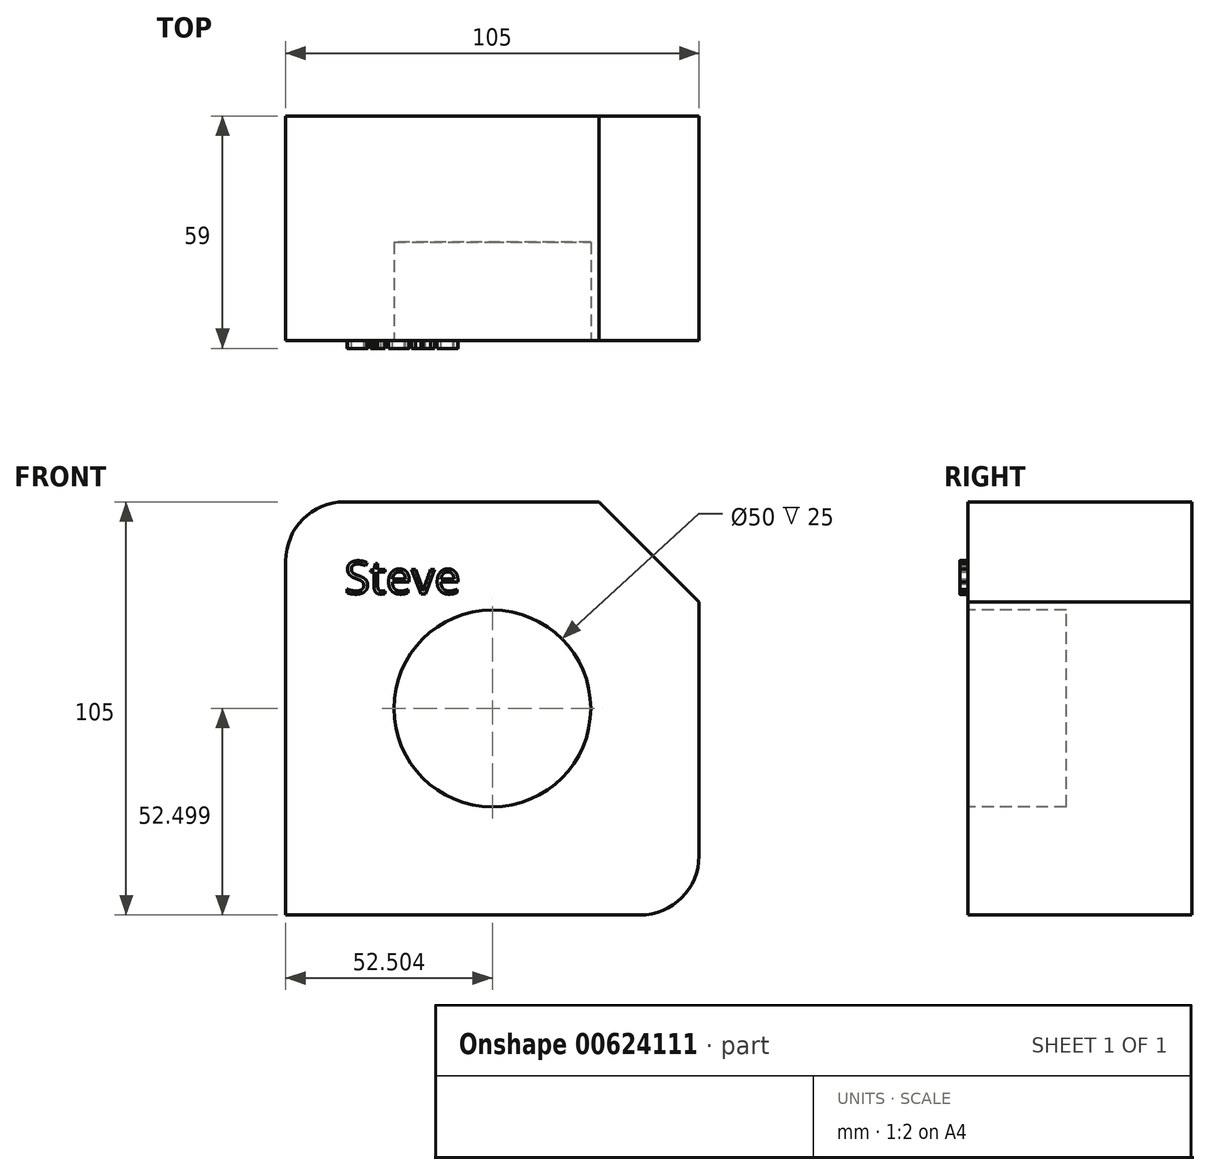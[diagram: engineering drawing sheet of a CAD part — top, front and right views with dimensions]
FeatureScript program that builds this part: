
annotation { "Feature Type Name" : "Feature", "Feature Type Description" : "" }
export const myFeature = defineFeature(function(context is Context, id is Id, definition is map)
    precondition{}
    {
        {
            var Q0;
            Q0=qCreatedBy(makeId("Front.planeOp"),FACE);
            var sketch = newSketch(context, id + "F0", { "sketchPlane" : qUnion([Q0])});
            skLineSegment(sketch, "E0.bottom", {"start": v(-33.87, 50.29) * mm, "end": v(30.73, 50.29) * mm});
            skLineSegment(sketch, "E0.top", {"start": v(-48.87, -54.71) * mm, "end": v(41.13, -54.71) * mm});
            skLineSegment(sketch, "E0.left", {"start": v(-48.87, 35.29) * mm, "end": v(-48.87, -54.71) * mm});
            skLineSegment(sketch, "E0.right", {"start": v(56.13, 24.88) * mm, "end": v(56.13, -39.71) * mm});
            skPoint(sketch, "E1.visualSharp", {"position": v(-48.87, 50.29) * mm});
            skArc(sketch, "E1.filletArc", {"start": v(-33.87, 50.29) * mm, "mid": v(-44.47, 45.9) * mm, "end": v(-48.87, 35.29) * mm});
            skPoint(sketch, "E2.visualSharp", {"position": v(56.13, -54.71) * mm});
            skArc(sketch, "E2.filletArc", {"start": v(41.13, -54.71) * mm, "mid": v(51.74, -50.32) * mm, "end": v(56.13, -39.71) * mm});
            skLineSegment(sketch, "E3", {"start": v(30.73, 50.29) * mm, "end": v(56.13, 24.88) * mm});
            skPoint(sketch, "E4.orphan", {"position": v(56.13, 50.29) * mm});
            skSolve(sketch);
        }
        {
            var Q0;
            Q0 = qSketchRegion(id + "F0", true);
            extrude(context, id + "F1", {"entities" : qUnion([Q0]), "depth" : 57 * mm, "offsetDistance" : 25 * mm});
        }
        {
            var Q0;
            Q0=makeQuery(id+"F1.opExtrude","CAP_FACE",FACE,{"disambiguationData":[OSD([sQuery(id+"F0.wireOp",EDGE,"E0.bottom"),sQuery(id+"F0.wireOp",EDGE,"E0.top"),sQuery(id+"F0.wireOp",EDGE,"E0.left"),sQuery(id+"F0.wireOp",EDGE,"E0.right"),sQuery(id+"F0.wireOp",EDGE,"E1.filletArc"),sQuery(id+"F0.wireOp",EDGE,"E2.filletArc"),sQuery(id+"F0.wireOp",EDGE,"E3")])],"isStart":false});
            var sketch = newSketch(context, id + "F2", { "sketchPlane" : qUnion([Q0])});
            skCircle(sketch, "E5", {"center": v(3.63, -2.21) * mm, "radius": 25 * mm});
            skSolve(sketch);
        }
        {
            var Q0;
            Q0 = qSketchRegion(id + "F2", true);
            extrude(context, id + "F3", {"entities" : qUnion([Q0]), "operationType" : NewBodyOperationType.REMOVE, "oppositeDirection" : true, "depth" : 25 * mm, "offsetDistance" : 25 * mm});
        }
        {
            var Q0;
            Q0=makeQuery(id+"F1.opExtrude","CAP_FACE",FACE,{"disambiguationData":[OSD([sQuery(id+"F0.wireOp",EDGE,"E0.bottom"),sQuery(id+"F0.wireOp",EDGE,"E0.top"),sQuery(id+"F0.wireOp",EDGE,"E0.left"),sQuery(id+"F0.wireOp",EDGE,"E0.right"),sQuery(id+"F0.wireOp",EDGE,"E1.filletArc"),sQuery(id+"F0.wireOp",EDGE,"E2.filletArc"),sQuery(id+"F0.wireOp",EDGE,"E3")])],"isStart":false});
            var sketch = newSketch(context, id + "F4", { "sketchPlane" : qUnion([Q0])});
            skText(sketch, "E6", { "text": "Steve", "fontName": "OpenSans-Regular.ttf"});
            const initialGuessF4  = {"E6": [-0.03387, 0.02692, 1, 0, 0.00837]};
            skSetInitialGuess(sketch, initialGuessF4);
            skSolve(sketch);
        }
        {
            var Q0;
            Q0 = qSketchRegion(id + "F4", true);
            extrude(context, id + "F5", {"entities" : qUnion([Q0]), "operationType" : NewBodyOperationType.ADD, "depth" : 2 * mm, "offsetDistance" : 25 * mm});
        }
    });
